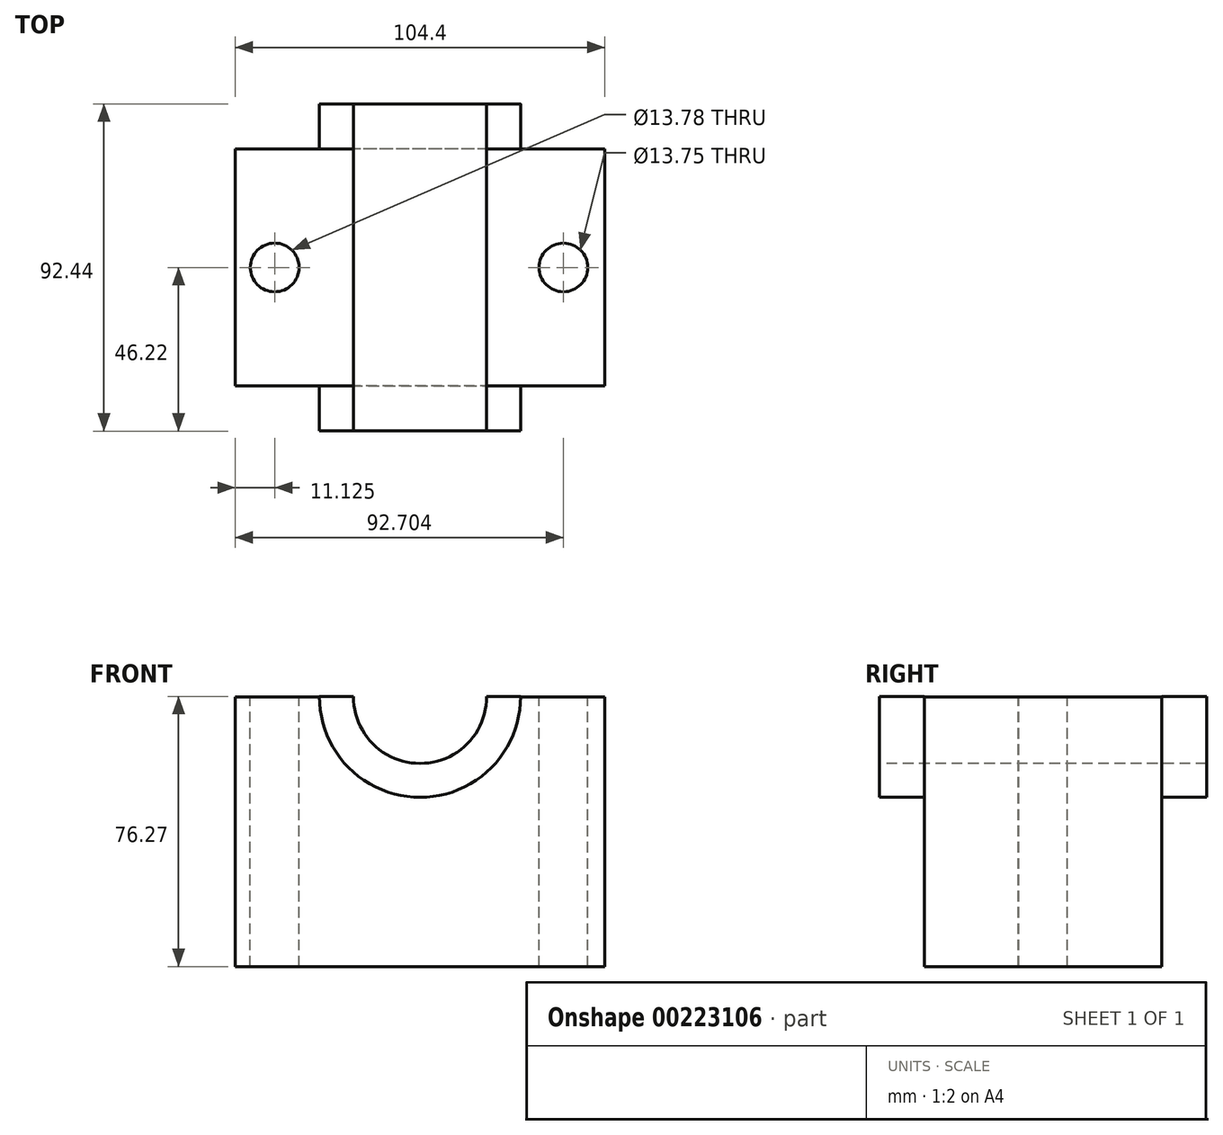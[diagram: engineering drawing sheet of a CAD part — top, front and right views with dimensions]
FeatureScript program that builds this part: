
annotation { "Feature Type Name" : "Feature", "Feature Type Description" : "" }
export const myFeature = defineFeature(function(context is Context, id is Id, definition is map)
    precondition{}
    {
        {
            var Q0;
            Q0=qCreatedBy(makeId("Top.planeOp"),FACE);
            var sketch = newSketch(context, id + "F0", { "sketchPlane" : qUnion([Q0])});
            skLineSegment(sketch, "E0.bottom", {"start": v(52.2, 33.52) * mm, "end": v(-52.2, 33.52) * mm});
            skLineSegment(sketch, "E0.top", {"start": v(52.2, -33.52) * mm, "end": v(-52.2, -33.52) * mm});
            skLineSegment(sketch, "E0.left", {"start": v(52.2, 33.52) * mm, "end": v(52.2, -33.52) * mm});
            skLineSegment(sketch, "E0.right", {"start": v(-52.2, 33.52) * mm, "end": v(-52.2, -33.52) * mm});
            skPoint(sketch, "E0.middle", {"position": v(0, 0) * mm});
            skSolve(sketch);
        }
        {
            var Q0;
            Q0 = qSketchRegion(id + "F0", true);
            extrude(context, id + "F1", {"entities" : qUnion([Q0]), "depth" : 76.2 * mm});
        }
        {
            var Q0;
            Q0=makeQuery(id+"F1.opExtrude","SWEPT_FACE",FACE,{"disambiguationData":[OSD([sQuery(id+"F0.wireOp",EDGE,"E0.top")])]});
            var sketch = newSketch(context, id + "F2", { "sketchPlane" : qUnion([Q0])});
            skCircle(sketch, "E1", {"center": v(0, 76.2) * mm, "radius": 28.4 * mm});
            skSolve(sketch);
        }
        {
            var Q0;
            Q0 = qSketchRegion(id + "F2", true);
            extrude(context, id + "F3", {"entities" : qUnion([Q0]), "operationType" : NewBodyOperationType.ADD, "depth" : 12.7 * mm});
        }
        {
            var Q0;
            Q0=makeQuery(id+"F1.opExtrude","SWEPT_FACE",FACE,{"disambiguationData":[OSD([sQuery(id+"F0.wireOp",EDGE,"E0.bottom")])]});
            var sketch = newSketch(context, id + "F4", { "sketchPlane" : qUnion([Q0])});
            skCircle(sketch, "E2", {"center": v(0, 76.2) * mm, "radius": 28.41 * mm});
            skSolve(sketch);
        }
        {
            var Q0;
            Q0 = qSketchRegion(id + "F4", true);
            extrude(context, id + "F5", {"entities" : qUnion([Q0]), "operationType" : NewBodyOperationType.ADD, "depth" : 12.7 * mm});
        }
        {
            var Q0;
            Q0=makeQuery(id+"F3.opExtrude","CAP_FACE",FACE,{"disambiguationData":[OSD([sQuery(id+"F2.wireOp",EDGE,"E1")])],"isStart":false});
            var sketch = newSketch(context, id + "F6", { "sketchPlane" : qUnion([Q0])});
            skCircle(sketch, "E3", {"center": v(0, 76.2) * mm, "radius": 18.82 * mm});
            skSolve(sketch);
        }
        {
            var Q0;
            Q0 = qSketchRegion(id + "F6", true);
            extrude(context, id + "F7", {"entities" : qUnion([Q0]), "operationType" : NewBodyOperationType.REMOVE, "oppositeDirection" : true, "depth" : 127 * mm});
        }
        {
            var Q0;
            Q0=makeQuery(id+"F3.opExtrude","CAP_FACE",FACE,{"disambiguationData":[OSD([sQuery(id+"F2.wireOp",EDGE,"E1")])],"isStart":false});
            var sketch = newSketch(context, id + "F8", { "sketchPlane" : qUnion([Q0])});
            skLineSegment(sketch, "E4", {"start": v(-28.8, 76.27) * mm, "end": v(30.38, 76.27) * mm});
            skSolve(sketch);
        }
        {
            var Q0;
            {var subQ0=sQuery(id+"F8.wireOp",EDGE,"E4");var subQ1=makeQuery(id+"F3.opExtrude","CAP_EDGE",EDGE,{"disambiguationData":[OSD([sQuery(id+"F2.wireOp",EDGE,"E1")])],"isStart":false});var subQ2=makeQuery(id+"F8.imprint","INTERSECT",VERTEX,{"disambiguationData":[OD(0.0)],"derivedFrom":[subQ1,subQ0]});Q0=makeQuery(id+"F8.imprint","IMPRINT",FACE,{"disambiguationData":[TD([[makeQuery(id+"F8.imprint","IMPRINT",EDGE,{"disambiguationData":[TD([[subQ2,-1.0]])],"derivedFrom":subQ0}),1.0]])]});}
            extrude(context, id + "F9", {"entities" : qUnion([Q0]), "operationType" : NewBodyOperationType.REMOVE, "oppositeDirection" : true, "depth" : 127 * mm});
        }
        {
            var Q0;
            {var subQ0=sQuery(id+"F0.wireOp",EDGE,"E0.right");var subQ2=sQuery(id+"F0.wireOp",EDGE,"E0.top");var subQ3=sQuery(id+"F0.wireOp",EDGE,"E0.bottom");Q0=makeQuery(id+"F7.boolean.opBoolean","SPLIT",FACE,{"disambiguationData":[TD([makeQuery(id+"F1.opExtrude","SWEPT_FACE",FACE,{"disambiguationData":[OSD([subQ0])]})])],"derivedFrom":makeQuery(id+"F1.opExtrude","CAP_FACE",FACE,{"disambiguationData":[OSD([subQ3,subQ2,sQuery(id+"F0.wireOp",EDGE,"E0.left"),subQ0])],"isStart":false})});}
            var sketch = newSketch(context, id + "F10", { "sketchPlane" : qUnion([Q0])});
            skCircle(sketch, "E5", {"center": v(-41.07, 0) * mm, "radius": 6.89 * mm});
            skSolve(sketch);
        }
        {
            var Q0;
            Q0 = qSketchRegion(id + "F10", true);
            extrude(context, id + "F11", {"entities" : qUnion([Q0]), "operationType" : NewBodyOperationType.REMOVE, "oppositeDirection" : true, "depth" : 127 * mm});
        }
        {
            var Q0;
            {var subQ0=sQuery(id+"F0.wireOp",EDGE,"E0.left");var subQ2=sQuery(id+"F0.wireOp",EDGE,"E0.top");var subQ3=sQuery(id+"F0.wireOp",EDGE,"E0.bottom");Q0=makeQuery(id+"F7.boolean.opBoolean","SPLIT",FACE,{"disambiguationData":[TD([makeQuery(id+"F1.opExtrude","SWEPT_FACE",FACE,{"disambiguationData":[OSD([subQ0])]})])],"derivedFrom":makeQuery(id+"F1.opExtrude","CAP_FACE",FACE,{"disambiguationData":[OSD([subQ3,subQ2,subQ0,sQuery(id+"F0.wireOp",EDGE,"E0.right")])],"isStart":false})});}
            var sketch = newSketch(context, id + "F12", { "sketchPlane" : qUnion([Q0])});
            skCircle(sketch, "E6", {"center": v(40.5, 0) * mm, "radius": 6.87 * mm});
            skSolve(sketch);
        }
        {
            var Q0;
            Q0 = qSketchRegion(id + "F12", true);
            extrude(context, id + "F13", {"entities" : qUnion([Q0]), "operationType" : NewBodyOperationType.REMOVE, "oppositeDirection" : true, "depth" : 127 * mm});
        }
    });
